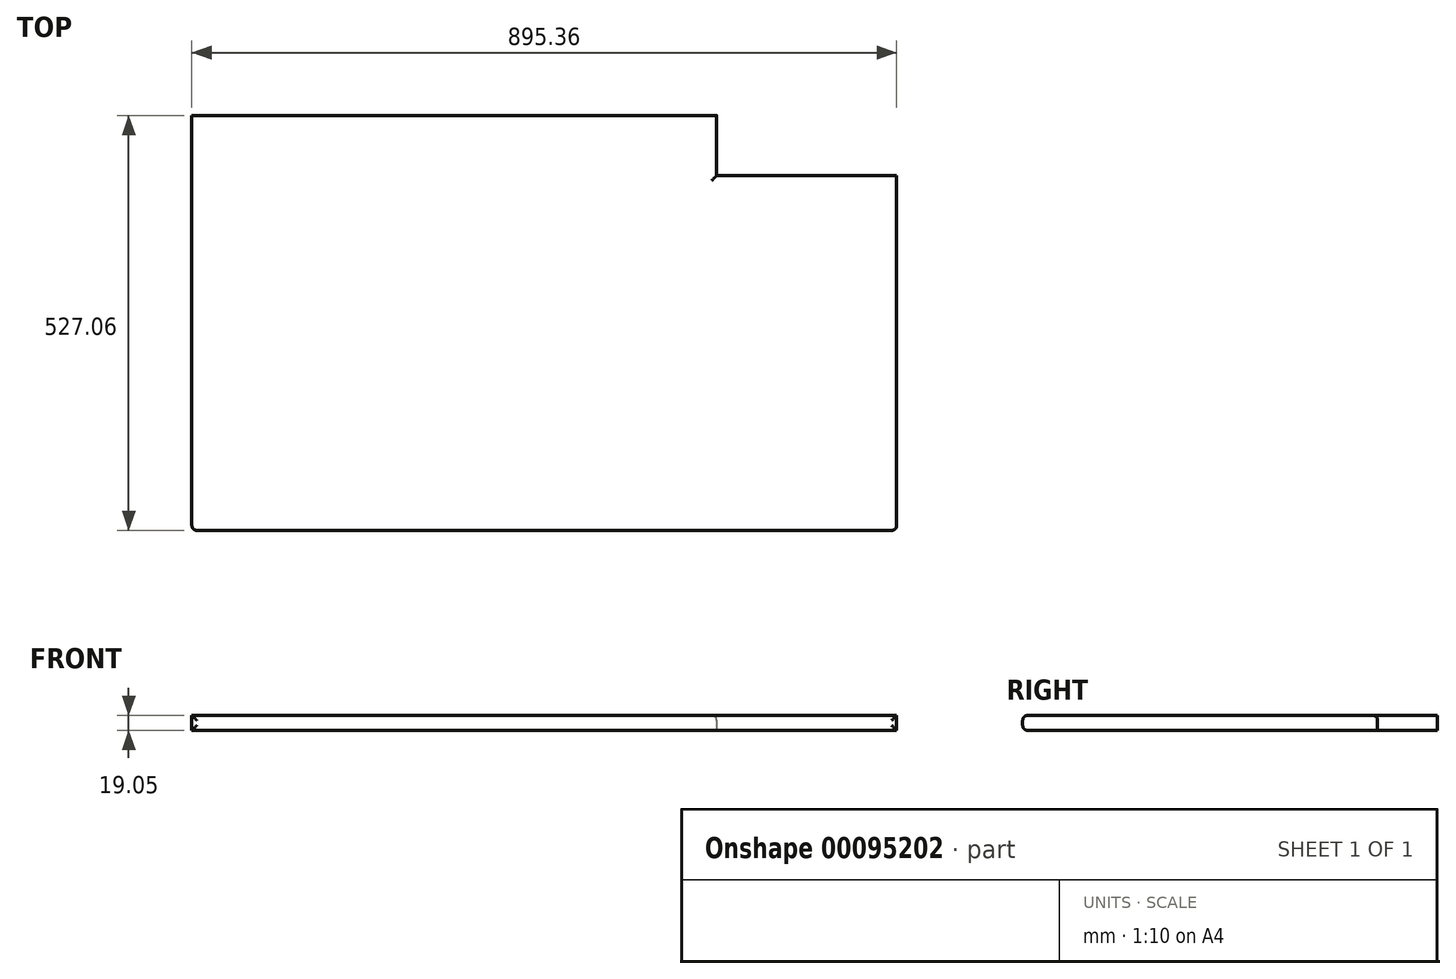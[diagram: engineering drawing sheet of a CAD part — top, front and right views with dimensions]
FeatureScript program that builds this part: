
annotation { "Feature Type Name" : "Feature", "Feature Type Description" : "" }
export const myFeature = defineFeature(function(context is Context, id is Id, definition is map)
    precondition{}
    {
        {
            var Q0;
            Q0=qCreatedBy(makeId("Top.planeOp"),FACE);
            var sketch = newSketch(context, id + "F0", { "sketchPlane" : qUnion([Q0])});
            skLineSegment(sketch, "E0.bottom", {"start": v(447.68, -263.52) * mm, "end": v(-447.68, -263.53) * mm});
            skLineSegment(sketch, "E0.top", {"start": v(447.68, 263.53) * mm, "end": v(-447.68, 263.53) * mm});
            skLineSegment(sketch, "E0.left", {"start": v(447.68, -263.53) * mm, "end": v(447.68, 263.53) * mm});
            skLineSegment(sketch, "E0.right", {"start": v(-447.68, -263.53) * mm, "end": v(-447.68, 263.53) * mm});
            skPoint(sketch, "E0.middle", {"position": v(0, 0) * mm});
            skLineSegment(sketch, "E1.bottom", {"start": v(447.68, 263.53) * mm, "end": v(219.07, 263.53) * mm});
            skLineSegment(sketch, "E1.top", {"start": v(447.68, 187.33) * mm, "end": v(219.07, 187.33) * mm});
            skLineSegment(sketch, "E1.left", {"start": v(447.68, 263.53) * mm, "end": v(447.68, 187.33) * mm});
            skLineSegment(sketch, "E1.right", {"start": v(219.07, 263.53) * mm, "end": v(219.07, 187.33) * mm});
            skSolve(sketch);
        }
        {
            var Q0;
            Q0=makeQuery(id+"F0.imprint","IMPRINT",FACE,{"disambiguationData":[TD([[makeQuery(id+"F0.imprint","IMPRINT",EDGE,{"derivedFrom":sQuery(id+"F0.wireOp",EDGE,"E0.bottom")}),-1.0]])]});
            extrude(context, id + "F1", {"entities" : qUnion([Q0]), "depth" : 19.05 * mm});
        }
        {
            var Q0;
            Q0=makeQuery(id+"F1.opExtrude","CAP_EDGE",EDGE,{"disambiguationData":[OSD([sQuery(id+"F0.wireOp",EDGE,"E0.bottom")])],"isStart":false});
            var Q1;
            Q1=makeQuery(id+"F1.opExtrude","CAP_EDGE",EDGE,{"disambiguationData":[OSD([sQuery(id+"F0.wireOp",EDGE,"E0.bottom")])],"isStart":true});
            var Q2;
            Q2=makeQuery(id+"F1.opExtrude","SWEPT_EDGE",EDGE,{"disambiguationData":[OSD([sQuery(id+"F0.wireOp",EDGE,"E0.bottom"),sQuery(id+"F0.wireOp",EDGE,"E0.right")])]});
            var Q3;
            Q3=makeQuery(id+"F1.opExtrude","SWEPT_EDGE",EDGE,{"disambiguationData":[OSD([sQuery(id+"F0.wireOp",EDGE,"E0.bottom"),sQuery(id+"F0.wireOp",EDGE,"E0.left")])]});
            var Q4;
            Q4=makeQuery(id+"F1.opExtrude","CAP_EDGE",EDGE,{"disambiguationData":[OSD([sQuery(id+"F0.wireOp",EDGE,"E1.right")])],"isStart":false});
            var Q5;
            Q5=makeQuery(id+"F1.opExtrude","CAP_EDGE",EDGE,{"disambiguationData":[OSD([sQuery(id+"F0.wireOp",EDGE,"E1.top")])],"isStart":false});
            fillet(context, id + "F2", {"entities" : qUnion([Q0, Q1, Q2, Q3, Q4, Q5]), "radius" : 6.35 * mm, "tangentPropagation" : true, "allowEdgeOverflow" : false});
        }
    });
